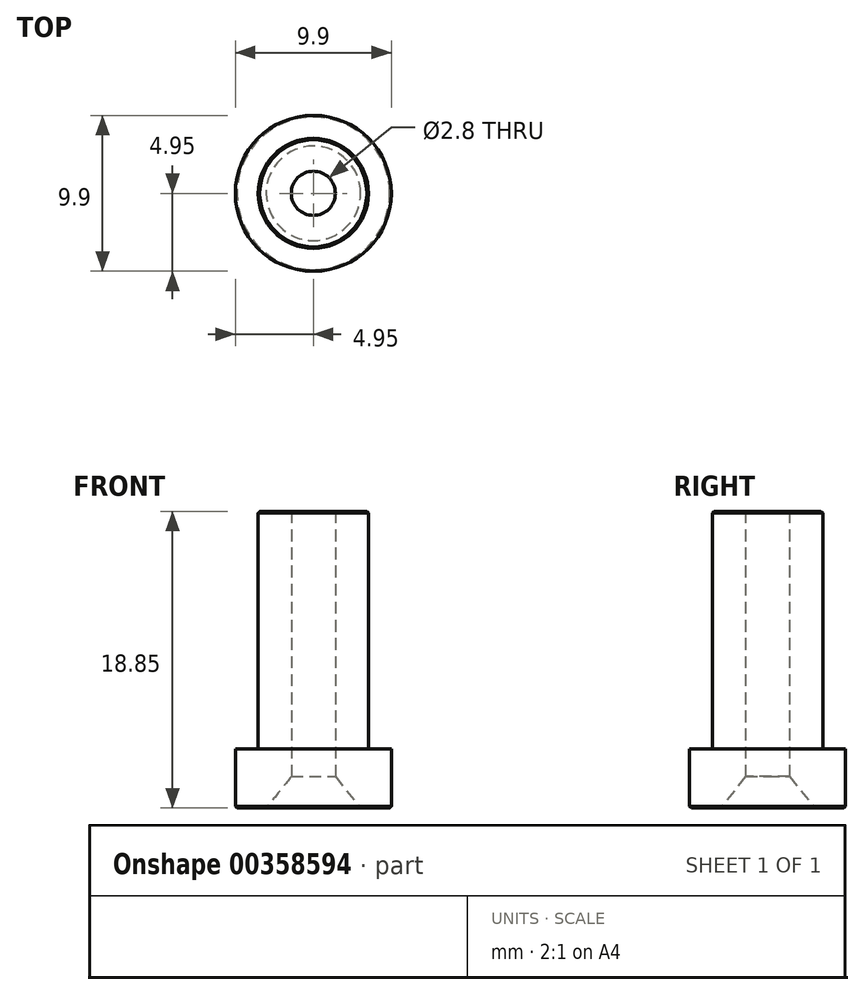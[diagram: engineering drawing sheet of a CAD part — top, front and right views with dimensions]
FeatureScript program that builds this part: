
annotation { "Feature Type Name" : "Feature", "Feature Type Description" : "" }
export const myFeature = defineFeature(function(context is Context, id is Id, definition is map)
    precondition{}
    {
        {
            var Q0;
            Q0=qCreatedBy(makeId("Right.planeOp"),FACE);
            var sketch = newSketch(context, id + "F0", { "sketchPlane" : qUnion([Q0])});
            skLineSegment(sketch, "E0", {"start": v(1.4, 2) * mm, "end": v(1.4, 18.85) * mm});
            skLineSegment(sketch, "E1", {"start": v(1.4, 18.85) * mm, "end": v(3.5, 18.85) * mm});
            skLineSegment(sketch, "E2", {"start": v(3.5, 18.85) * mm, "end": v(3.5, 3.75) * mm});
            skLineSegment(sketch, "E3", {"start": v(3.5, 3.75) * mm, "end": v(4.95, 3.75) * mm});
            skLineSegment(sketch, "E4", {"start": v(4.95, 3.75) * mm, "end": v(4.95, 0) * mm});
            skLineSegment(sketch, "E5", {"start": v(4.95, 0) * mm, "end": v(3, 0) * mm});
            skLineSegment(sketch, "E6", {"start": v(0, 0) * mm, "end": v(0, 22.08) * mm});
            skLineSegment(sketch, "E7", {"start": v(3, 0) * mm, "end": v(1.4, 2) * mm});
            skPoint(sketch, "E8.orphan", {"position": v(1.4, 0) * mm});
            skSolve(sketch);
        }
        {
            var Q0;
            Q0 = qSketchRegion(id + "F0", true);
            var Q1;
            Q1=sQuery(id+"F0.wireOp",EDGE,"E6");
            revolve(context, id + "F1", {"entities" : qUnion([Q0]), "axis" : qUnion([Q1]), "revolveType" : RevolveType.FULL});
        }
        {
            var Q0;
            Q0=makeQuery(id+"F1.opRevolve","SWEPT_EDGE",EDGE,{"disambiguationData":[OSD([sQuery(id+"F0.wireOp",EDGE,"E4"),sQuery(id+"F0.wireOp",EDGE,"E5")])]});
            var Q1;
            Q1=makeQuery(id+"F1.opRevolve","SWEPT_EDGE",EDGE,{"disambiguationData":[OSD([sQuery(id+"F0.wireOp",EDGE,"E1"),sQuery(id+"F0.wireOp",EDGE,"E2")])]});
            chamfer(context, id + "F2", {"entities" : qUnion([Q0, Q1]), "width" : .1 * mm, "tangentPropagation" : true});
        }
    });
